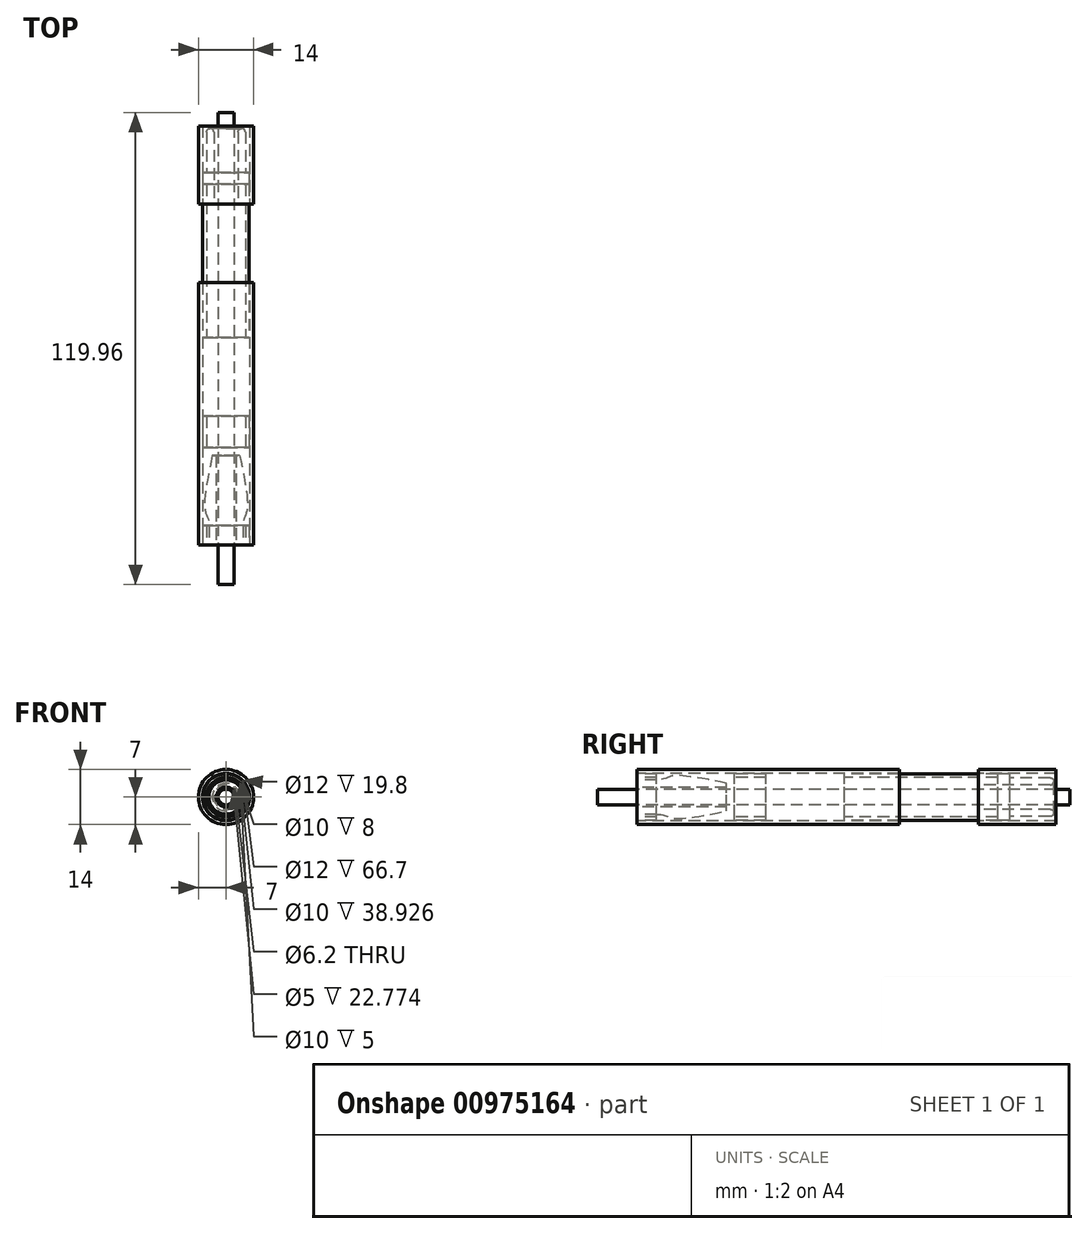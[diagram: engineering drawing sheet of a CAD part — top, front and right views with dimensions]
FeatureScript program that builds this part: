
annotation { "Feature Type Name" : "Feature", "Feature Type Description" : "" }
export const myFeature = defineFeature(function(context is Context, id is Id, definition is map)
    precondition{}
    {
        {
            var Q0;
            Q0=qCreatedBy(makeId("Right.planeOp"),FACE);
            var sketch = newSketch(context, id + "F0", { "sketchPlane" : qUnion([Q0])});
            skLineSegment(sketch, "E0.bottom", {"start": v(-10, 0) * mm, "end": v(109.96, 0) * mm});
            skLineSegment(sketch, "E0.top", {"start": v(-10, 2) * mm, "end": v(109.96, 2) * mm});
            skLineSegment(sketch, "E0.left", {"start": v(-10, 0) * mm, "end": v(-10, 2) * mm});
            skLineSegment(sketch, "E0.right", {"start": v(109.96, 0) * mm, "end": v(109.96, 2) * mm});
            skPoint(sketch, "E1", {"position": v(-10, 2.5) * mm});
            skPoint(sketch, "E2", {"position": v(-10, 6) * mm});
            skPoint(sketch, "E3", {"position": v(-10, 5.9) * mm});
            skPoint(sketch, "E4", {"position": v(-10, 5) * mm});
            skPoint(sketch, "E5", {"position": v(-10, 7) * mm});
            skLineSegment(sketch, "E6", {"start": v(0, 4.35) * mm, "end": v(5, 4.35) * mm});
            skFitSpline(sketch, "E7", {"points": [v(5, 4.35) * mm, v(10, 5.45) * mm, v(30, 2) * mm], "startDerivative": vector(22.43, 0) * mm, "endDerivative": vector(4.5, 0) * mm});
            skFitSpline(sketch, "E8.0", {"points": [v(5, 4.9) * mm, v(5.44, 4.9) * mm, v(6.14, 4.97) * mm, v(6.87, 5.18) * mm, v(7.54, 5.48) * mm, v(8.23, 5.74) * mm, v(8.93, 5.9) * mm, v(9.54, 5.98) * mm, v(10.25, 6) * mm, v(11.35, 5.98) * mm, v(12.96, 5.83) * mm, v(15.19, 5.51) * mm, v(17.6, 5.1) * mm, v(20.1, 4.62) * mm, v(22.55, 4.11) * mm, v(24.85, 3.62) * mm, v(26.55, 3.25) * mm, v(27.71, 3) * mm, v(28.48, 2.83) * mm, v(29.01, 2.72) * mm, v(29.37, 2.65) * mm, v(29.6, 2.6) * mm, v(29.78, 2.58) * mm, v(29.9, 2.56) * mm, v(29.97, 2.55) * mm, v(30, 2.55) * mm, v(30, 2.55) * mm, v(30, 2.55) * mm, v(30.02, 2.55) * mm, v(30.03, 2.55) * mm, v(30.04, 2.55) * mm, v(30.05, 2.55) * mm]});
            skLineSegment(sketch, "E8.1", {"start": v(0, 4.9) * mm, "end": v(5, 4.9) * mm});
            skLineSegment(sketch, "E9.bottom", {"start": v(0, 7) * mm, "end": v(66.7, 7) * mm});
            skLineSegment(sketch, "E9.top", {"start": v(0, 6) * mm, "end": v(66.7, 6) * mm});
            skLineSegment(sketch, "E9.left", {"start": v(0, 7) * mm, "end": v(0, 6) * mm});
            skLineSegment(sketch, "E9.right", {"start": v(66.7, 7) * mm, "end": v(66.7, 6) * mm});
            skLineSegment(sketch, "E10", {"start": v(0, 4.35) * mm, "end": v(0, 2.5) * mm});
            skLineSegment(sketch, "E11", {"start": v(0, 2.5) * mm, "end": v(22.77, 2.5) * mm});
            skLineSegment(sketch, "E12", {"start": v(22.77, 2.5) * mm, "end": v(22.77, 3.5) * mm});
            skLineSegment(sketch, "E13.bottom", {"start": v(0, 5.9) * mm, "end": v(5, 5.9) * mm});
            skLineSegment(sketch, "E13.top", {"start": v(0, 5) * mm, "end": v(5, 5) * mm});
            skLineSegment(sketch, "E13.left", {"start": v(0, 5.9) * mm, "end": v(0, 5) * mm});
            skLineSegment(sketch, "E13.right", {"start": v(5, 5.9) * mm, "end": v(5, 5) * mm});
            skLineSegment(sketch, "E14", {"start": v(0, 4.9) * mm, "end": v(0, 4.35) * mm});
            skLineSegment(sketch, "E15", {"start": v(18.62, 4.9) * mm, "end": v(18.62, 5.9) * mm});
            skLineSegment(sketch, "E16", {"start": v(18.62, 5.9) * mm, "end": v(24.77, 5.9) * mm});
            skLineSegment(sketch, "E17", {"start": v(24.77, 5.9) * mm, "end": v(24.77, 4.9) * mm});
            skLineSegment(sketch, "E18", {"start": v(30, 2.55) * mm, "end": v(90, 2.55) * mm});
            skLineSegment(sketch, "E19.bottom", {"start": v(24.77, 5.9) * mm, "end": v(32.77, 5.9) * mm});
            skLineSegment(sketch, "E19.top", {"start": v(24.77, 5) * mm, "end": v(32.77, 5) * mm});
            skLineSegment(sketch, "E19.right", {"start": v(32.77, 5.9) * mm, "end": v(32.77, 5) * mm});
            skArc(sketch, "E20", {"start": v(95, 5.5) * mm, "mid": v(94.7, 5.2) * mm, "end": v(95, 4.9) * mm});
            skLineSegment(sketch, "E21", {"start": v(95, 5.5) * mm, "end": v(105, 5.5) * mm});
            skLineSegment(sketch, "E22", {"start": v(95, 4.9) * mm, "end": v(105, 4.9) * mm});
            skArc(sketch, "E23", {"start": v(105, 4.9) * mm, "mid": v(105.9, 4) * mm, "end": v(105, 3.1) * mm});
            skArc(sketch, "E24", {"start": v(105, 5.5) * mm, "mid": v(106.5, 4) * mm, "end": v(105, 2.5) * mm});
            skLineSegment(sketch, "E25", {"start": v(105, 3.1) * mm, "end": v(95, 3.1) * mm});
            skLineSegment(sketch, "E26", {"start": v(105, 2.5) * mm, "end": v(95, 2.5) * mm});
            skLineSegment(sketch, "E27", {"start": v(95, 2.5) * mm, "end": v(90, 2) * mm});
            skLineSegment(sketch, "E28", {"start": v(90, 2.55) * mm, "end": v(95, 3.1) * mm});
            skLineSegment(sketch, "E29.bottom", {"start": v(86.7, 7) * mm, "end": v(106.5, 7) * mm});
            skLineSegment(sketch, "E29.top", {"start": v(86.7, 6) * mm, "end": v(106.5, 6) * mm});
            skLineSegment(sketch, "E29.left", {"start": v(86.7, 7) * mm, "end": v(86.7, 6) * mm});
            skLineSegment(sketch, "E29.right", {"start": v(106.5, 7) * mm, "end": v(106.5, 6) * mm});
            skPoint(sketch, "E30", {"position": v(106.5, 4) * mm});
            skLineSegment(sketch, "E31.bottom", {"start": v(52.77, 5.9) * mm, "end": v(91.7, 5.9) * mm});
            skLineSegment(sketch, "E31.top", {"start": v(52.77, 5) * mm, "end": v(91.7, 5) * mm});
            skLineSegment(sketch, "E31.left", {"start": v(52.77, 5.9) * mm, "end": v(52.77, 5) * mm});
            skLineSegment(sketch, "E31.right", {"start": v(91.7, 5.9) * mm, "end": v(91.7, 5) * mm});
            skLineSegment(sketch, "E32", {"start": v(66.7, 7) * mm, "end": v(86.7, 7) * mm, "construction": true});
            skLineSegment(sketch, "E33", {"start": v(32.77, 5) * mm, "end": v(52.77, 5) * mm, "construction": true});
            skLineSegment(sketch, "E34", {"start": v(100, 4.9) * mm, "end": v(100, 3.1) * mm, "construction": true});
            skLineSegment(sketch, "E35", {"start": v(95, 3.1) * mm, "end": v(86.7, 3.1) * mm});
            skLineSegment(sketch, "E36", {"start": v(86.7, 3.1) * mm, "end": v(86.7, 5) * mm});
            skLineSegment(sketch, "E37", {"start": v(24.77, 4.9) * mm, "end": v(32.77, 4.9) * mm});
            skLineSegment(sketch, "E38", {"start": v(32.77, 4.9) * mm, "end": v(32.77, 3) * mm});
            skLineSegment(sketch, "E39", {"start": v(32.77, 3) * mm, "end": v(27.7, 3) * mm});
            skLineSegment(sketch, "E40", {"start": v(91.7, 5.9) * mm, "end": v(94.7, 5.9) * mm});
            skLineSegment(sketch, "E41", {"start": v(94.7, 5.9) * mm, "end": v(94.7, 4.9) * mm});
            skLineSegment(sketch, "E42", {"start": v(94.7, 4.9) * mm, "end": v(95, 4.9) * mm});
            skSolve(sketch);
        }
        {
            var Q0;
            Q0=makeQuery(id+"F0.imprint","IMPRINT",FACE,{"disambiguationData":[TD([[makeQuery(id+"F0.imprint","IMPRINT",EDGE,{"derivedFrom":sQuery(id+"F0.wireOp",EDGE,"E0.bottom")}),1.0]])]});
            var Q1;
            Q1=makeQuery(id+"F0.imprint","IMPRINT",FACE,{"disambiguationData":[TD([[makeQuery(id+"F0.imprint","IMPRINT",EDGE,{"derivedFrom":sQuery(id+"F0.wireOp",EDGE,"E13.bottom")}),-1.0]])]});
            var Q2;
            {var subQ1=sQuery(id+"F0.wireOp",EDGE,"E6");Q2=makeQuery(id+"F0.imprint","IMPRINT",FACE,{"disambiguationData":[TD([[makeQuery(id+"F0.imprint","IMPRINT",EDGE,{"derivedFrom":subQ1}),-1.0]])]});}
            var Q3;
            {var subQ3=sQuery(id+"F0.wireOp",EDGE,"E15");Q3=makeQuery(id+"F0.imprint","IMPRINT",FACE,{"disambiguationData":[TD([[makeQuery(id+"F0.imprint","IMPRINT",EDGE,{"derivedFrom":subQ3}),-1.0]])]});}
            var Q4;
            {var subQ5=sQuery(id+"F0.wireOp",EDGE,"E31.bottom");Q4=makeQuery(id+"F0.imprint","IMPRINT",FACE,{"disambiguationData":[TD([[makeQuery(id+"F0.imprint","IMPRINT",EDGE,{"derivedFrom":subQ5}),-1.0]])]});}
            var Q5;
            Q5=makeQuery(id+"F0.imprint","IMPRINT",FACE,{"disambiguationData":[TD([[makeQuery(id+"F0.imprint","IMPRINT",EDGE,{"derivedFrom":sQuery(id+"F0.wireOp",EDGE,"E29.bottom")}),-1.0]])]});
            var Q6;
            Q6=sQuery(id+"F0.wireOp",EDGE,"E0.bottom");
            revolve(context, id + "F1", {"surfaceOperationType" : NewSurfaceOperationType.NEW, "entities" : qUnion([Q0, Q1, Q2, Q3, Q4, Q5]), "axis" : qUnion([Q6]), "revolveType" : RevolveType.FULL});
        }
        {
            var Q0;
            {var subQ16=sQuery(id+"F0.wireOp",EDGE,"E6");Q0=makeQuery(id+"F0.imprint","IMPRINT",FACE,{"disambiguationData":[TD([[makeQuery(id+"F0.imprint","IMPRINT",EDGE,{"derivedFrom":subQ16}),1.0]])]});}
            var Q1;
            {var subQ0=sQuery(id+"F0.wireOp",EDGE,"E19.bottom");Q1=makeQuery(id+"F0.imprint","IMPRINT",FACE,{"disambiguationData":[TD([[makeQuery(id+"F0.imprint","IMPRINT",EDGE,{"derivedFrom":subQ0}),-1.0]])]});}
            var Q2;
            Q2=sQuery(id+"F0.wireOp",EDGE,"E0.bottom");
            revolve(context, id + "F2", {"surfaceOperationType" : NewSurfaceOperationType.NEW, "entities" : qUnion([Q0, Q1]), "axis" : qUnion([Q2]), "revolveType" : RevolveType.FULL});
        }
        {
            var Q0;
            Q0=makeQuery(id+"F0.imprint","IMPRINT",FACE,{"disambiguationData":[TD([[makeQuery(id+"F0.imprint","IMPRINT",EDGE,{"derivedFrom":sQuery(id+"F0.wireOp",EDGE,"E9.bottom")}),-1.0]])]});
            var Q1;
            Q1=makeQuery(id+"F0.imprint","IMPRINT",FACE,{"disambiguationData":[TD([[makeQuery(id+"F0.imprint","IMPRINT",EDGE,{"derivedFrom":sQuery(id+"F0.wireOp",EDGE,"E22")}),-1.0]])]});
            var Q2;
            Q2=sQuery(id+"F0.wireOp",EDGE,"E0.bottom");
            revolve(context, id + "F3", {"surfaceOperationType" : NewSurfaceOperationType.NEW, "entities" : qUnion([Q0, Q1]), "axis" : qUnion([Q2]), "revolveType" : RevolveType.FULL});
        }
    });
